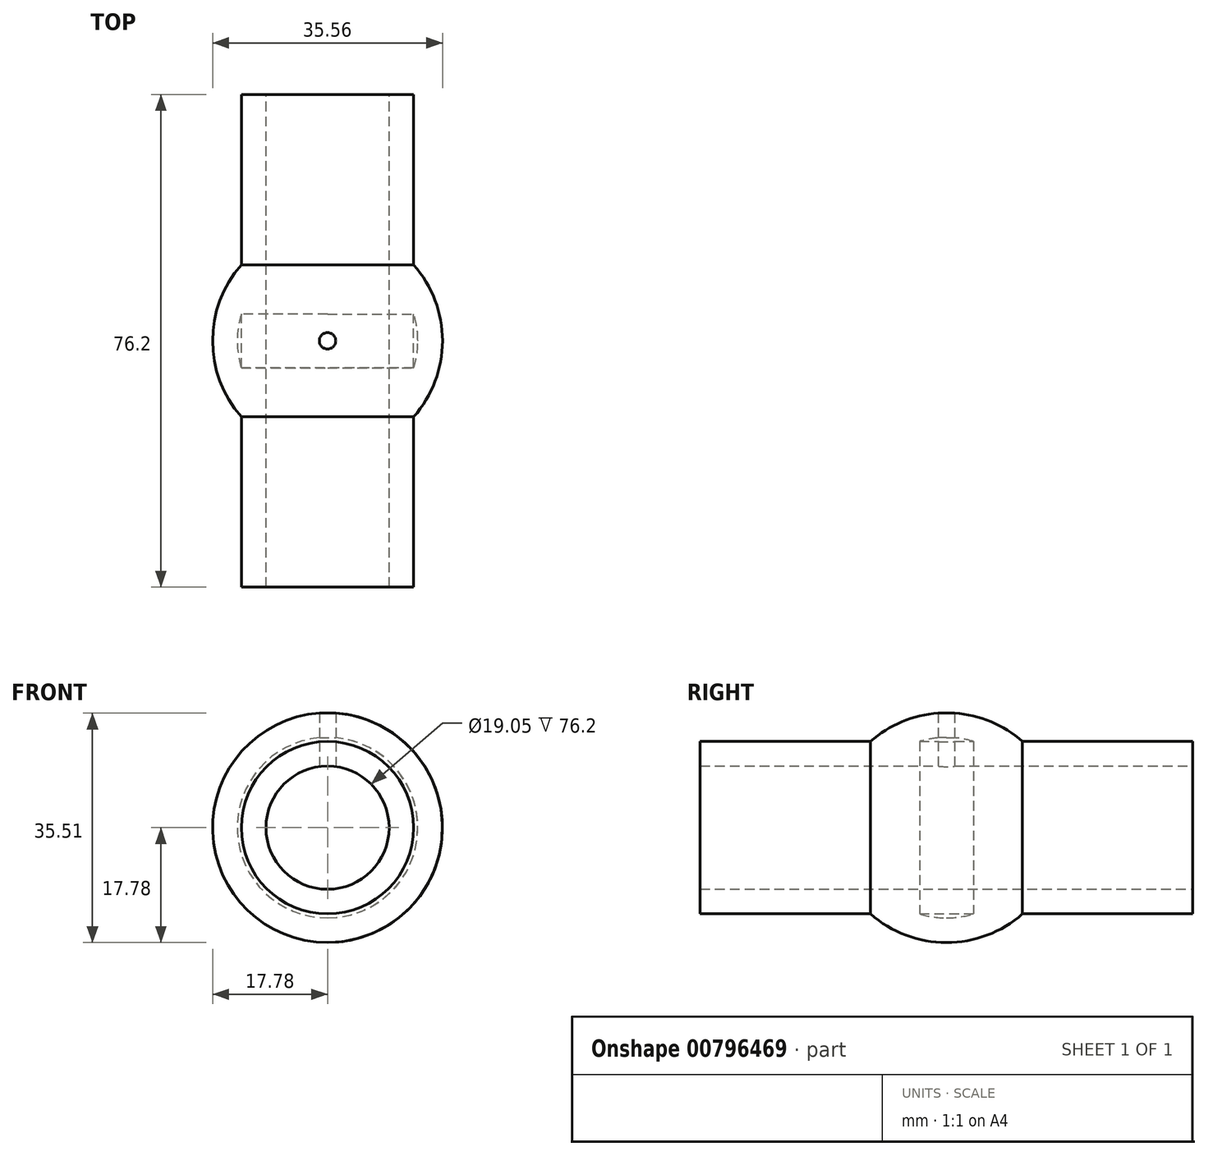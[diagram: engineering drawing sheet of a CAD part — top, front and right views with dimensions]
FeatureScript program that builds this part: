
annotation { "Feature Type Name" : "Feature", "Feature Type Description" : "" }
export const myFeature = defineFeature(function(context is Context, id is Id, definition is map)
    precondition{}
    {
        {
            var Q0;
            Q0=qCreatedBy(makeId("Front.planeOp"),FACE);
            var sketch = newSketch(context, id + "F0", { "sketchPlane" : qUnion([Q0])});
            skCircle(sketch, "E0", {"center": v(0, 0) * mm, "radius": 13.97 * mm});
            skCircle(sketch, "E1.0", {"center": v(0, 0) * mm, "radius": 17.78 * mm});
            skLineSegment(sketch, "E2", {"start": v(0, 17.78) * mm, "end": v(0, -17.78) * mm});
            skSolve(sketch);
        }
        {
            var Q0;
            {var subQ0=sQuery(id+"F0.wireOp",EDGE,"E2");var subQ1=sQuery(id+"F0.wireOp",EDGE,"E0");var subQ2=makeQuery(id+"F0.imprint","INTERSECT",VERTEX,{"disambiguationData":[OD(0.0)],"derivedFrom":[subQ1,subQ0]});Q0=makeQuery(id+"F0.imprint","IMPRINT",FACE,{"disambiguationData":[TD([[makeQuery(id+"F0.imprint","IMPRINT",EDGE,{"disambiguationData":[TD([[subQ2,-1.0]])],"derivedFrom":subQ1}),-1.0]])]});}
            var Q1;
            Q1=sQuery(id+"F0.wireOp",EDGE,"E2");
            revolve(context, id + "F1", {"surfaceOperationType" : NewSurfaceOperationType.NEW, "entities" : qUnion([Q0]), "axis" : qUnion([Q1]), "revolveType" : RevolveType.FULL});
        }
        {
            var Q0;
            Q0=qCreatedBy(makeId("Front.planeOp"),FACE);
            var sketch = newSketch(context, id + "F2", { "sketchPlane" : qUnion([Q0])});
            skCircle(sketch, "E3", {"center": v(0, 0) * mm, "radius": 9.53 * mm});
            skCircle(sketch, "E4.0", {"center": v(0, 0) * mm, "radius": 13.33 * mm});
            skSolve(sketch);
        }
        {
            var Q0;
            Q0 = qSketchRegion(id + "F2", true);
            extrude(context, id + "F3", {"entities" : qUnion([Q0]), "operationType" : NewBodyOperationType.ADD, "endBound" : BoundingType.SYMMETRIC, "depth" : 76.2 * mm, "offsetDistance" : 25.4 * mm});
        }
        {
            var Q0;
            Q0=sQuery(id+"F0.wireOp",VERTEX,"E0.center");
            var Q1;
            Q1=makeQuery(id+"F1.opRevolve","SWEPT_BODY",BODY,{"disambiguationData":[OSD([sQuery(id+"F0.wireOp",EDGE,"E0"),sQuery(id+"F0.wireOp",EDGE,"E1.0"),sQuery(id+"F0.wireOp",EDGE,"E2")])]});
            hole(context, id + "F4", {"style" : HoleStyle.SIMPLE, "endStyle" : HoleEndStyle.BLIND, "holeDiameter" : 19.05 * mm, "majorDiameter" : 6.35 * mm, "holeDepth" : 25.4 * mm, "isTappedThrough" : true, "tappedDepth" : 12.7 * mm, "tapClearance" : 3, "locations" : qUnion([Q0]), "scope" : qUnion([Q1])});
        }
        {
            var Q0;
            Q0=sQuery(id+"F0.wireOp",VERTEX,"E0.center");
            var Q1;
            Q1=makeQuery(id+"F1.opRevolve","SWEPT_BODY",BODY,{"disambiguationData":[OSD([sQuery(id+"F0.wireOp",EDGE,"E0"),sQuery(id+"F0.wireOp",EDGE,"E1.0"),sQuery(id+"F0.wireOp",EDGE,"E2")])]});
            hole(context, id + "F5", {"style" : HoleStyle.SIMPLE, "endStyle" : HoleEndStyle.BLIND, "oppositeDirection" : true, "holeDiameter" : 19.05 * mm, "majorDiameter" : 6.35 * mm, "holeDepth" : 25.4 * mm, "isTappedThrough" : true, "tappedDepth" : 12.7 * mm, "tapClearance" : 3, "locations" : qUnion([Q0]), "scope" : qUnion([Q1])});
        }
        {
            var Q0;
            Q0=qCreatedBy(makeId("Top.planeOp"),FACE);
            var sketch = newSketch(context, id + "F6", { "sketchPlane" : qUnion([Q0])});
            skCircle(sketch, "E5", {"center": v(0, 0) * mm, "radius": 4.68 * mm});
            skSolve(sketch);
        }
        {
            var Q0;
            Q0=sQuery(id+"F6.wireOp",VERTEX,"E5.center");
            var Q1;
            Q1=makeQuery(id+"F1.opRevolve","SWEPT_BODY",BODY,{"disambiguationData":[OSD([sQuery(id+"F0.wireOp",EDGE,"E0"),sQuery(id+"F0.wireOp",EDGE,"E1.0"),sQuery(id+"F0.wireOp",EDGE,"E2")])]});
            hole(context, id + "F7", {"style" : HoleStyle.SIMPLE, "endStyle" : HoleEndStyle.BLIND, "oppositeDirection" : true, "holeDiameter" : 2.54 * mm, "majorDiameter" : 6.35 * mm, "holeDepth" : 25.4 * mm, "isTappedThrough" : true, "tappedDepth" : 12.7 * mm, "tapClearance" : 3, "locations" : qUnion([Q0]), "scope" : qUnion([Q1])});
        }
    });
